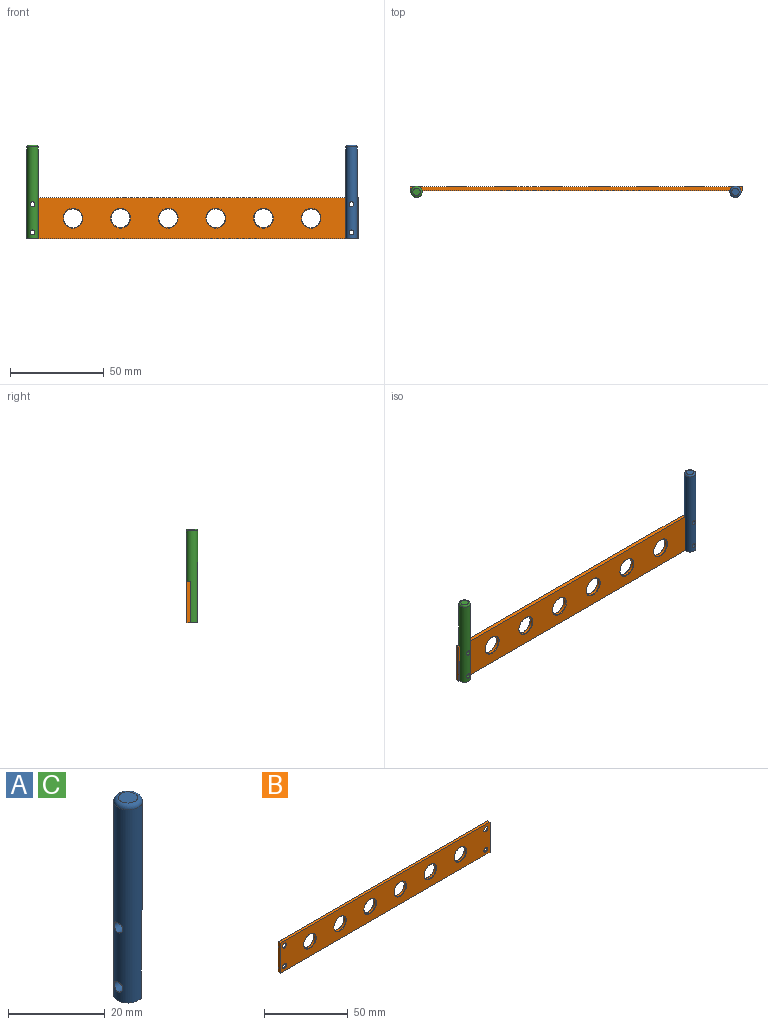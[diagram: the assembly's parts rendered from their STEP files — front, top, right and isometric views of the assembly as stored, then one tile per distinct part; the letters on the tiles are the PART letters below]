
ASSEMBLY  parts=3 mates=1
PART A: 8 faces, bbox 6.5x6.5x50 mm
  f0: cylinder r=3mm len=49mm, axis (0,0,-1), area 751.1mm2, adj f1,f3,f4,f5,f6,f7
  f1: plane 6x4mm, normal (0,0,-1), area 20mm2, adj f0,f5
  f2: plane 4x4mm, normal (0,0,1), area 12.6mm2, adj f3
  f3: torus R=2mm, axis (0,0,1), area 26mm2, adj f0,f2
  f4: plane 5.66x2mm, normal (0,0,-1), area 8.3mm2, adj f0,f5
  f5: plane 22x5.66mm, normal (1,0,0), area 114.6mm2, adj f0,f1,f4,f6,f7
  f6: cylinder r=1.25mm len=4mm, axis (1,0,0), area 30.4mm2, adj f0,f5
  f7: cylinder r=1.25mm len=4mm, axis (1,0,0), area 30.4mm2, adj f0,f5
PART B: 32 faces, bbox 177x2x22 mm
  f0: plane 177x2mm, normal (0,0,1), area 354mm2, adj f1,f3,f4,f5
  f1: plane 22x2mm, normal (-1,0,0), area 44mm2, adj f0,f2,f4,f5
  f2: plane 177x2mm, normal (0,0,-1), area 354mm2, adj f1,f3,f4,f5
  f3: plane 22x2mm, normal (1,0,0), area 44mm2, adj f0,f2,f4,f5
  f4: plane 177x22mm, normal (0,-1,0), area 3340.2mm2, adj f0,f1,f2,f3,f12,f14,f16,f18
  f5: plane 177x22mm, normal (0,1,0), area 3232.6mm2, adj f0,f1,f2,f3,f13,f15,f17,f19
  f6: cylinder r=5mm len=10mm, axis (0,1,0), area 47.1mm2, adj f20,f31
  f7: cylinder r=5mm len=10mm, axis (0,1,0), area 47.1mm2, adj f29,f30
  f8: cylinder r=5mm len=10mm, axis (0,1,0), area 47.1mm2, adj f27,f28
  f9: cylinder r=5mm len=10mm, axis (0,1,0), area 47.1mm2, adj f25,f26
  f10: cylinder r=5mm len=10mm, axis (0,1,0), area 47.1mm2, adj f23,f24
  f11: cylinder r=5mm len=10mm, axis (0,1,0), area 47.1mm2, adj f21,f22
  f12: cylinder r=1.65mm len=3.3mm, axis (0,1,0), area 3mm2, adj f4,f13
  f13: cone r=1.65mm half-angle=45deg, axis (0,1,0), area 38.1mm2, adj f5,f12
  f14: cylinder r=1.65mm len=3.3mm, axis (0,1,0), area 3mm2, adj f4,f15
  f15: cone r=1.65mm half-angle=45deg, axis (0,1,0), area 38.1mm2, adj f5,f14
  f16: cylinder r=1.65mm len=3.3mm, axis (0,1,0), area 3mm2, adj f4,f17
  f17: cone r=1.65mm half-angle=45deg, axis (0,1,0), area 38.1mm2, adj f5,f16
  f18: cylinder r=1.65mm len=3.3mm, axis (0,1,0), area 3mm2, adj f4,f19
  f19: cone r=1.65mm half-angle=45deg, axis (0,1,0), area 38.1mm2, adj f5,f18
  f20: cone r=5mm half-angle=45deg, axis (0,1,0), area 11.4mm2, adj f5,f6
  f21: cone r=5.25mm half-angle=45deg, axis (0,-1,0), area 11.4mm2, adj f4,f11
  f22: cone r=5mm half-angle=45deg, axis (0,1,0), area 11.4mm2, adj f5,f11
  f23: cone r=5mm half-angle=45deg, axis (0,1,0), area 11.4mm2, adj f5,f10
  f24: cone r=5.25mm half-angle=45deg, axis (0,-1,0), area 11.4mm2, adj f4,f10
  f25: cone r=5.25mm half-angle=45deg, axis (0,-1,0), area 11.4mm2, adj f4,f9
  f26: cone r=5mm half-angle=45deg, axis (0,1,0), area 11.4mm2, adj f5,f9
  f27: cone r=5mm half-angle=45deg, axis (0,1,0), area 11.4mm2, adj f5,f8
  f28: cone r=5.25mm half-angle=45deg, axis (0,-1,0), area 11.4mm2, adj f4,f8
  f29: cone r=5.25mm half-angle=45deg, axis (0,-1,0), area 11.4mm2, adj f4,f7
  f30: cone r=5mm half-angle=45deg, axis (0,1,0), area 11.4mm2, adj f5,f7
  f31: cone r=5.25mm half-angle=45deg, axis (0,-1,0), area 11.4mm2, adj f4,f6
PART C: same geometry as A
PLACE A rot(axis=(0,0,1),90deg) t=(75.23,4.58,6.9)mm
PLACE B t=(-98.27,7.29,6.9)mm
PLACE C rot(axis=(0,0,1),90deg) t=(-94.77,4.58,6.9)mm
MATE fastened B.f18 <-> A.f6  axis (0,1,0) through (75.23,5.58,10.4)mm
